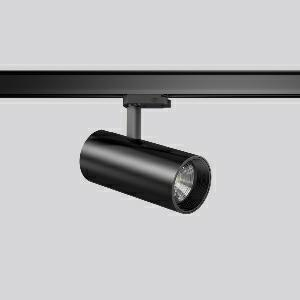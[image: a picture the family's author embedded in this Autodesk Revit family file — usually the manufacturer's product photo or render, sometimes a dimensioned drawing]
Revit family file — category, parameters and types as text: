
# Revit family: deecos_s_mini_742208_003_1_76_956f
name_source: partatom
category: Lighting Fixtures
units: mm (PartAtom-declared; Revit-internal decimal feet)

## family parameters
Cut with Voids When Loaded = No
Host = Face
Light Source = No
Part Type = Normal
Room Calculation Point = No
Round Connector Dimension = Use Diameter
Shared = No

## types (1)
- DEECOS S mini (1 x LED Modul 940, 3000 lm, 4000)
    Apparent Load = 29 VA
    Approval mark = CE
    CIE Flux Codes = 98 100 100 100 100
    Color Rendering = 92
    Color Temperature = 4000
    Default Elevation = 1800 mm
    Description = Series: DEECOS S mini
LED surface-mounted projector in modern design with no visible cooling ribs. Housing: die-cast aluminium, powder-coated. Rotation range: 356°. Swivel range: 90°. Black plastic ring and recessed LED to prevent glare from the side. Optical assembly with lens made of plastic (polycarbonate) for the best homogeneous light distribution - can be changed without tools. Best colour rendering index Ra>90. With adapter for RZB 3-circuit DALI tracks. Suitable for Track on ceiling, Wall track. High quality converter without flickering and stroboscopic effect. The following accessories can be mounted without use of tools: interchangeable lenses, decorative glasses, honeycomb louvre, clear and frosted diffusers, white interchangeable plastic ring. 
Colour: deep black, matt (RAL 9005)
Diameter: 87 mm
Height: 214 mm
Lamp: LED
Socket: without socket
Colour temperature: 4000K
Colour rendering index (CRI): 92
System power: 29 W
Rated luminous flux: 3000 lm
Luminous efficiency: 103 lm/W
Control gear: Converter, dimmable, DALI
Protection class: I
Type of protection: IP 20
    Height = 214 mm
    Lamp = 1 x LED Modul 940
    Lamp Light Flux = 3000 lm
    Lamp count = 1
    Length = 87 mm
    Lifetime = 50000 h
    Luminous efficacy = 103 lm/W
    Manufacturer = RZB
    ModVariant = No
    Model = 742208.003.1.76
    Mounting Place = Ceiling
    Mounting Type = Rail mounted
    Number of Poles = 1
    OnlyDefault = Yes
    Power Factor = 1
    Product Name = DEECOS S mini
    Product group = Track mounted projectors
    ProductGroupID = 301
    Protection Class = Protection class I
    Protection Degree = IP 20
    RLX_Detail_Level = 1
    RLX_Emergency_Light_Flux = 0 lm
    RLX_Emergency_Type = 0
    RLX_Emergency_Type_DB = No
    RlxData = <blob elided: 38825 chars, md5=0e394577>
    Socket = socket
    Standby Power = 0 W
    System Light Flux = 3000 lm
    System Power = 29 W
    Type Comments = Product without accessories
    Type Image = 741930.003.jpg
    URL = http://relux.com
    VarID = ---
    Voltage = 230 V
    Voltage Range = 220-240 V
    Weight = 0.00 kg
    Width = 0 mm  [stored 0 ft]

note: [stored X ft] marks values corroborated as IEEE doubles in the binary element streams (Revit-internal decimal feet)

## geometry (parser evidence)
native form markers: Blend x4, Sweep x15
no freeform markers — native parametric forms only
